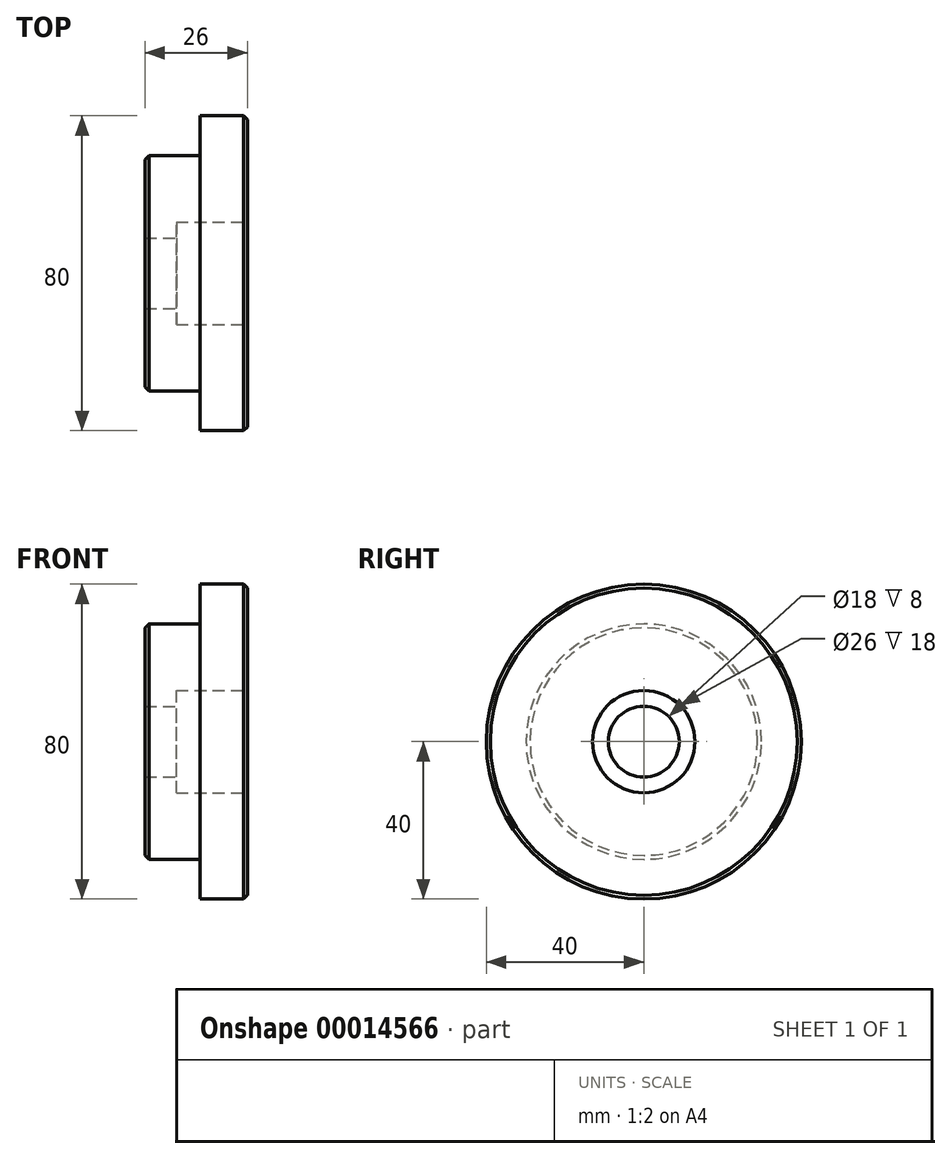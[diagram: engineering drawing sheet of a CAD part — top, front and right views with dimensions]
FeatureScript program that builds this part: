
annotation { "Feature Type Name" : "Feature", "Feature Type Description" : "" }
export const myFeature = defineFeature(function(context is Context, id is Id, definition is map)
    precondition{}
    {
        {
            var Q0;
            Q0=qCreatedBy(makeId("Right.planeOp"),FACE);
            var sketch = newSketch(context, id + "F0", { "sketchPlane" : qUnion([Q0])});
            skCircle(sketch, "E0", {"center": v(0, 0) * mm, "radius": 40 * mm});
            skSolve(sketch);
        }
        {
            var Q0;
            Q0=qSketchRegion(id+"F0",true);
            extrude(context, id + "F1", {"entities" : qUnion([Q0]), "depth" : 12 * mm});
        }
        {
            var Q0;
            Q0=makeQuery(id+"F1.opExtrude","CAP_FACE",FACE,{"disambiguationData":[OSD([sQuery(id+"F0.wireOp",EDGE,"E0")])],"isStart":true});
            var sketch = newSketch(context, id + "F2", { "sketchPlane" : qUnion([Q0])});
            skCircle(sketch, "E1", {"center": v(0, 0) * mm, "radius": 29.9 * mm});
            skSolve(sketch);
        }
        {
            var Q0;
            Q0=qSketchRegion(id+"F2",true);
            extrude(context, id + "F3", {"entities" : qUnion([Q0]), "operationType" : NewBodyOperationType.ADD, "depth" : 14 * mm});
        }
        {
            var Q0;
            Q0=makeQuery(id+"F3.opExtrude","CAP_EDGE",EDGE,{"disambiguationData":[OSD([sQuery(id+"F2.wireOp",EDGE,"E1")])],"isStart":false});
            var Q1;
            Q1=makeQuery(id+"F1.opExtrude","CAP_EDGE",EDGE,{"disambiguationData":[OSD([sQuery(id+"F0.wireOp",EDGE,"E0")])],"isStart":false});
            chamfer(context, id + "F4", {"entities" : qUnion([Q0, Q1]), "width" : 1 * mm, "tangentPropagation" : true});
        }
        {
            var Q0;
            Q0=makeQuery(id+"F1.opExtrude","CAP_FACE",FACE,{"disambiguationData":[OSD([sQuery(id+"F0.wireOp",EDGE,"E0")])],"isStart":false});
            var sketch = newSketch(context, id + "F5", { "sketchPlane" : qUnion([Q0])});
            skLineSegment(sketch, "E2", {"start": v(0, 0) * mm, "end": v(-51.58, 0) * mm, "construction": true});
            skSolve(sketch);
        }
        {
            var Q0;
            Q0=sQuery(id+"F5.wireOp",VERTEX,"E2.start");
            var Q1;
            Q1=makeQuery(id+"F1.opExtrude","SWEPT_BODY",BODY,{"disambiguationData":[OSD([sQuery(id+"F0.wireOp",EDGE,"E0")])]});
            hole(context, id + "F6", {"style" : HoleStyle.C_BORE, "holeDiameter" : 18 * mm, "cBoreDiameter" : 26 * mm, "cBoreDepth" : 18 * mm, "endStyle" : HoleEndStyle.THROUGH, "locations" : qUnion([Q0]), "scope" : qUnion([Q1])});
        }
    });
